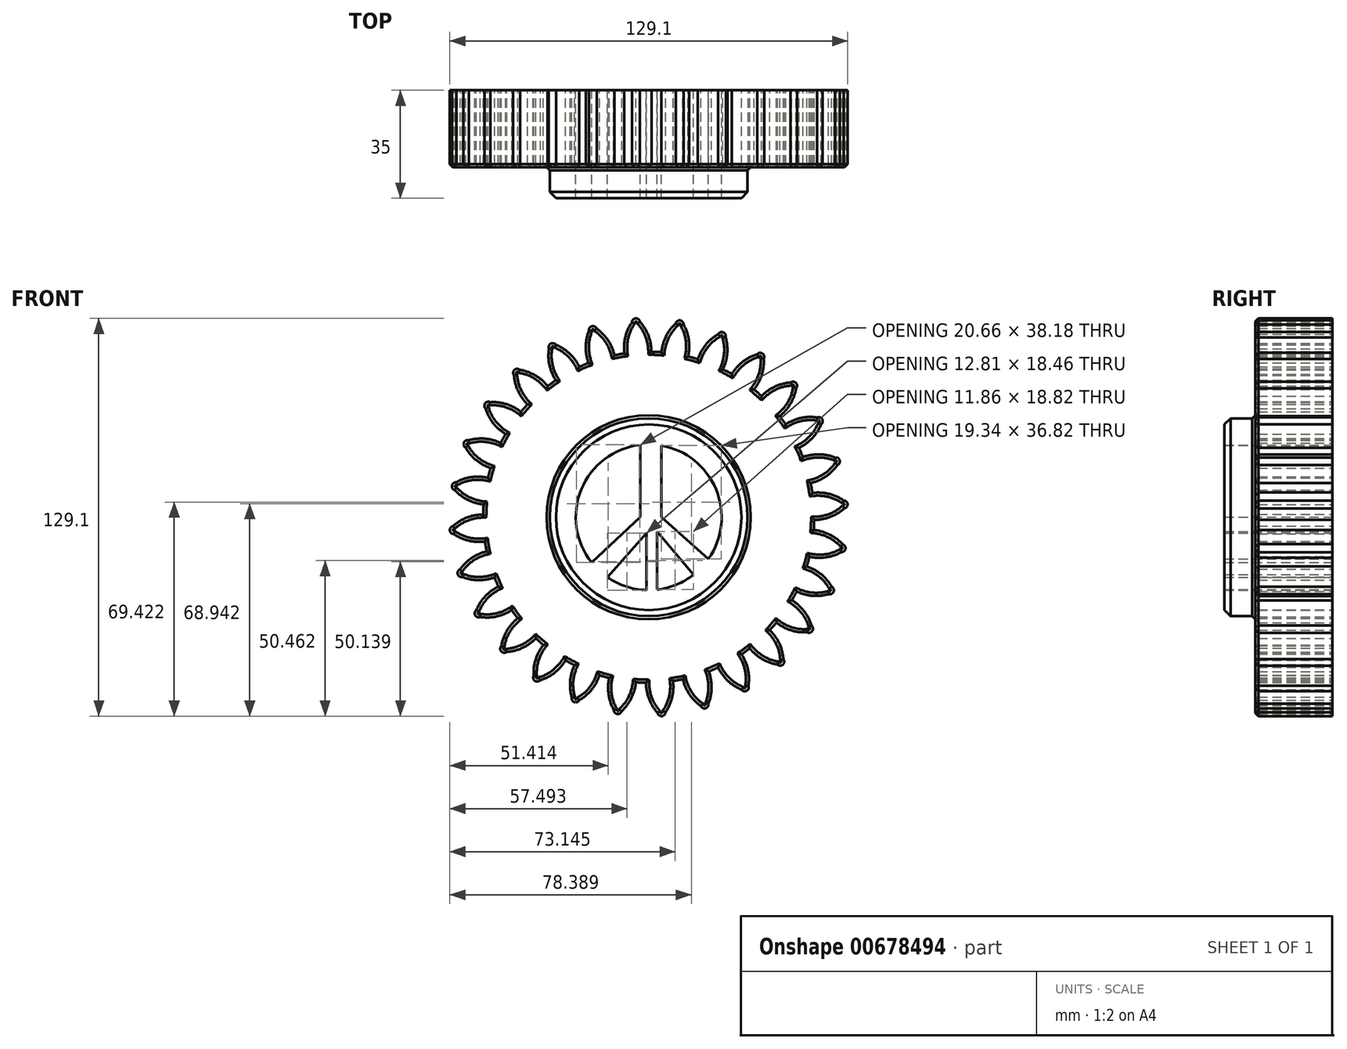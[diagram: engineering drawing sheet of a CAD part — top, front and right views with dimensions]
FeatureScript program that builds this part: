
annotation { "Feature Type Name" : "Feature", "Feature Type Description" : "" }
export const myFeature = defineFeature(function(context is Context, id is Id, definition is map)
    precondition{}
    {
        {
            var Q0;
            Q0=qCreatedBy(makeId("Front.planeOp"),FACE);
            var sketch = newSketch(context, id + "F0", { "sketchPlane" : qUnion([Q0])});
            skCircle(sketch, "E0", {"center": v(0, 0) * mm, "radius": 53.72 * mm});
            skCircle(sketch, "E1", {"center": v(0, 0) * mm, "radius": 58.67 * mm, "construction": true});
            skCircle(sketch, "E2", {"center": v(0, 0) * mm, "radius": 63.5 * mm, "construction": true});
            skLineSegment(sketch, "E3", {"start": v(0, 0) * mm, "end": v(0, 72.67) * mm, "construction": true});
            skLineSegment(sketch, "E4", {"start": v(0, 0) * mm, "end": v(-5.05, 77.02) * mm, "construction": true});
            skLineSegment(sketch, "E5", {"start": v(0, 58.67) * mm, "end": v(-57.47, 58.67) * mm, "construction": true});
            skLineSegment(sketch, "E6", {"start": v(0, 58.67) * mm, "end": v(-61.26, 36.38) * mm, "construction": true});
            skCircle(sketch, "E7", {"center": v(0, 0) * mm, "radius": 55.14 * mm, "construction": true});
            skCircle(sketch, "E8", {"center": v(0, 58.67) * mm, "radius": 14.6 * mm, "construction": true});
            skCircle(sketch, "E9", {"center": v(-13.72, 53.68) * mm, "radius": 14.6 * mm, "construction": true});
            skArc(sketch, "E10", {"start": v(0, 58.67) * mm, "mid": v(-1.19, 61.2) * mm, "end": v(-2.86, 63.44) * mm});
            skArc(sketch, "E11", {"start": v(0.88, 53.71) * mm, "mid": v(0.64, 56.23) * mm, "end": v(0, 58.67) * mm});
            skArc(sketch, "E12.MirrorCS", {"start": v(-7.66, 58.17) * mm, "mid": v(-6.8, 60.83) * mm, "end": v(-5.45, 63.27) * mm});
            skArc(sketch, "E13.MirrorCS", {"start": v(-7.88, 53.14) * mm, "mid": v(-7.98, 55.66) * mm, "end": v(-7.66, 58.17) * mm});
            skArc(sketch, "E14", {"start": v(-2.86, 63.44) * mm, "mid": v(-4.23, 64.55) * mm, "end": v(-5.45, 63.27) * mm});
            skCircle(sketch, "E15", {"center": v(0, 0) * mm, "radius": 32.11 * mm});
            skCircle(sketch, "E16", {"center": v(0, 0) * mm, "radius": 23.65 * mm});
            skLineSegment(sketch, "E17", {"start": v(4.17, 23.28) * mm, "end": v(4.17, 0) * mm});
            skLineSegment(sketch, "E18", {"start": v(4.17, 0) * mm, "end": v(19.4, -13.54) * mm});
            skLineSegment(sketch, "E19", {"start": v(-2.8, 23.48) * mm, "end": v(-2.8, 0) * mm});
            skLineSegment(sketch, "E20", {"start": v(-2.8, 0) * mm, "end": v(-18.53, -14.7) * mm});
            skLineSegment(sketch, "E21", {"start": v(-13.46, -19.44) * mm, "end": v(-0.65, -5.18) * mm});
            skLineSegment(sketch, "E22", {"start": v(-0.65, -5.18) * mm, "end": v(-0.65, -23.64) * mm});
            skLineSegment(sketch, "E23", {"start": v(2.67, -23.5) * mm, "end": v(2.67, -4.68) * mm});
            skLineSegment(sketch, "E24", {"start": v(2.67, -4.68) * mm, "end": v(14.52, -18.67) * mm});
            skSolve(sketch);
        }
        {
            var Q0;
            {var subQ0=sQuery(id+"F0.wireOp",EDGE,"E0");var subQ1=makeQuery(id+"F0.imprint","INTERSECT",VERTEX,{"derivedFrom":[subQ0,sQuery(id+"F0.wireOp",EDGE,"E11")]});Q0=makeQuery(id+"F0.imprint","IMPRINT",FACE,{"disambiguationData":[TD([[makeQuery(id+"F0.imprint","IMPRINT",EDGE,{"disambiguationData":[TD([[subQ1,-1.0]])],"derivedFrom":subQ0}),1.0]])]});}
            var Q1;
            Q1=makeQuery(id+"F0.imprint","IMPRINT",FACE,{"disambiguationData":[TD([[makeQuery(id+"F0.imprint","IMPRINT",EDGE,{"derivedFrom":sQuery(id+"F0.wireOp",EDGE,"E10")}),1.0]])]});
            extrude(context, id + "F1", {"entities" : qUnion([Q0, Q1]), "depth" : 25 * mm, "offsetDistance" : 25 * mm});
        }
        {
            var Q0;
            Q0=makeQuery(id+"F1.opExtrude","SWEPT_BODY",BODY,{"disambiguationData":[OSD([sQuery(id+"F0.wireOp",EDGE,"E0"),sQuery(id+"F0.wireOp",EDGE,"E10"),sQuery(id+"F0.wireOp",EDGE,"E11"),sQuery(id+"F0.wireOp",EDGE,"E12.MirrorCS"),sQuery(id+"F0.wireOp",EDGE,"E13.MirrorCS"),sQuery(id+"F0.wireOp",EDGE,"E14")])]});
            var Q1;
            Q1=makeQuery(id+"F1.opExtrude","SWEPT_FACE",FACE,{"disambiguationData":[OSD([sQuery(id+"F0.wireOp",EDGE,"E0")])]});
            circularPattern(context, id + "F2", {"entities" : qUnion([Q0]), "axis" : qUnion([Q1]), "angle" : 360 * degree, "instanceCount" : 28, "equalSpace" : true});
        }
        {
            var Q0;
            Q0=makeQuery(id+"F0.imprint","IMPRINT",FACE,{"disambiguationData":[TD([[makeQuery(id+"F0.imprint","IMPRINT",EDGE,{"derivedFrom":sQuery(id+"F0.wireOp",EDGE,"g40fDyrK-UICW-5EDt-5LR5-nAFWeNeGLo4p.bottom")}),-1.0]])]});
            var Q1;
            Q1=makeQuery(id+"F0.imprint","IMPRINT",FACE,{"disambiguationData":[TD([[makeQuery(id+"F0.imprint","IMPRINT",EDGE,{"derivedFrom":sQuery(id+"F0.wireOp",EDGE,"E15")}),1.0]])]});
            var Q2;
            {var subQ3=sQuery(id+"F0.wireOp",EDGE,"E17");Q2=makeQuery(id+"F0.imprint","IMPRINT",FACE,{"disambiguationData":[TD([[makeQuery(id+"F0.imprint","IMPRINT",EDGE,{"derivedFrom":subQ3}),-1.0]])]});}
            extrude(context, id + "F3", {"entities" : qUnion([Q0, Q1, Q2]), "operationType" : NewBodyOperationType.ADD, "depth" : 35 * mm, "offsetDistance" : 25 * mm});
        }
        {
            var Q0;
            Q0=makeQuery(id+"F3.opExtrude","CAP_EDGE",EDGE,{"disambiguationData":[OSD([sQuery(id+"F0.wireOp",EDGE,"E15")])],"isStart":false});
            chamfer(context, id + "F4", {"entities" : qUnion([Q0]), "width" : 2 * mm, "tangentPropagation" : true});
        }
        {
            var Q0;
            {var subQ0=makeQuery(id+"F1.opExtrude","CAP_FACE",FACE,{"disambiguationData":[OSD([sQuery(id+"F0.wireOp",EDGE,"E0"),sQuery(id+"F0.wireOp",EDGE,"E10"),sQuery(id+"F0.wireOp",EDGE,"E11"),sQuery(id+"F0.wireOp",EDGE,"E12.MirrorCS"),sQuery(id+"F0.wireOp",EDGE,"E13.MirrorCS"),sQuery(id+"F0.wireOp",EDGE,"E14"),sQuery(id+"F0.wireOp",EDGE,"E15")])],"isStart":false});Q0=makeQuery(id+"F3.boolean.opBoolean","MERGE",FACE,{"derivedFrom":[subQ0,makeQuery(id+"F2.opPattern","COPY",FACE,{"derivedFrom":subQ0,"instanceName":"1"}),makeQuery(id+"F2.opPattern","COPY",FACE,{"derivedFrom":subQ0,"instanceName":"2"}),makeQuery(id+"F2.opPattern","COPY",FACE,{"derivedFrom":subQ0,"instanceName":"3"}),makeQuery(id+"F2.opPattern","COPY",FACE,{"derivedFrom":subQ0,"instanceName":"4"}),makeQuery(id+"F2.opPattern","COPY",FACE,{"derivedFrom":subQ0,"instanceName":"5"}),makeQuery(id+"F2.opPattern","COPY",FACE,{"derivedFrom":subQ0,"instanceName":"6"}),makeQuery(id+"F2.opPattern","COPY",FACE,{"derivedFrom":subQ0,"instanceName":"7"}),makeQuery(id+"F2.opPattern","COPY",FACE,{"derivedFrom":subQ0,"instanceName":"8"}),makeQuery(id+"F2.opPattern","COPY",FACE,{"derivedFrom":subQ0,"instanceName":"9"}),makeQuery(id+"F2.opPattern","COPY",FACE,{"derivedFrom":subQ0,"instanceName":"10"}),makeQuery(id+"F2.opPattern","COPY",FACE,{"derivedFrom":subQ0,"instanceName":"11"}),makeQuery(id+"F2.opPattern","COPY",FACE,{"derivedFrom":subQ0,"instanceName":"12"}),makeQuery(id+"F2.opPattern","COPY",FACE,{"derivedFrom":subQ0,"instanceName":"13"}),makeQuery(id+"F2.opPattern","COPY",FACE,{"derivedFrom":subQ0,"instanceName":"14"}),makeQuery(id+"F2.opPattern","COPY",FACE,{"derivedFrom":subQ0,"instanceName":"15"}),makeQuery(id+"F2.opPattern","COPY",FACE,{"derivedFrom":subQ0,"instanceName":"16"}),makeQuery(id+"F2.opPattern","COPY",FACE,{"derivedFrom":subQ0,"instanceName":"17"}),makeQuery(id+"F2.opPattern","COPY",FACE,{"derivedFrom":subQ0,"instanceName":"18"}),makeQuery(id+"F2.opPattern","COPY",FACE,{"derivedFrom":subQ0,"instanceName":"19"}),makeQuery(id+"F2.opPattern","COPY",FACE,{"derivedFrom":subQ0,"instanceName":"20"}),makeQuery(id+"F2.opPattern","COPY",FACE,{"derivedFrom":subQ0,"instanceName":"21"}),makeQuery(id+"F2.opPattern","COPY",FACE,{"derivedFrom":subQ0,"instanceName":"22"}),makeQuery(id+"F2.opPattern","COPY",FACE,{"derivedFrom":subQ0,"instanceName":"23"}),makeQuery(id+"F2.opPattern","COPY",FACE,{"derivedFrom":subQ0,"instanceName":"24"}),makeQuery(id+"F2.opPattern","COPY",FACE,{"derivedFrom":subQ0,"instanceName":"25"}),makeQuery(id+"F2.opPattern","COPY",FACE,{"derivedFrom":subQ0,"instanceName":"26"}),makeQuery(id+"F2.opPattern","COPY",FACE,{"derivedFrom":subQ0,"instanceName":"27"})]});}
            chamfer(context, id + "F5", {"entities" : qUnion([Q0]), "width" : 1 * mm, "tangentPropagation" : true});
        }
    });
